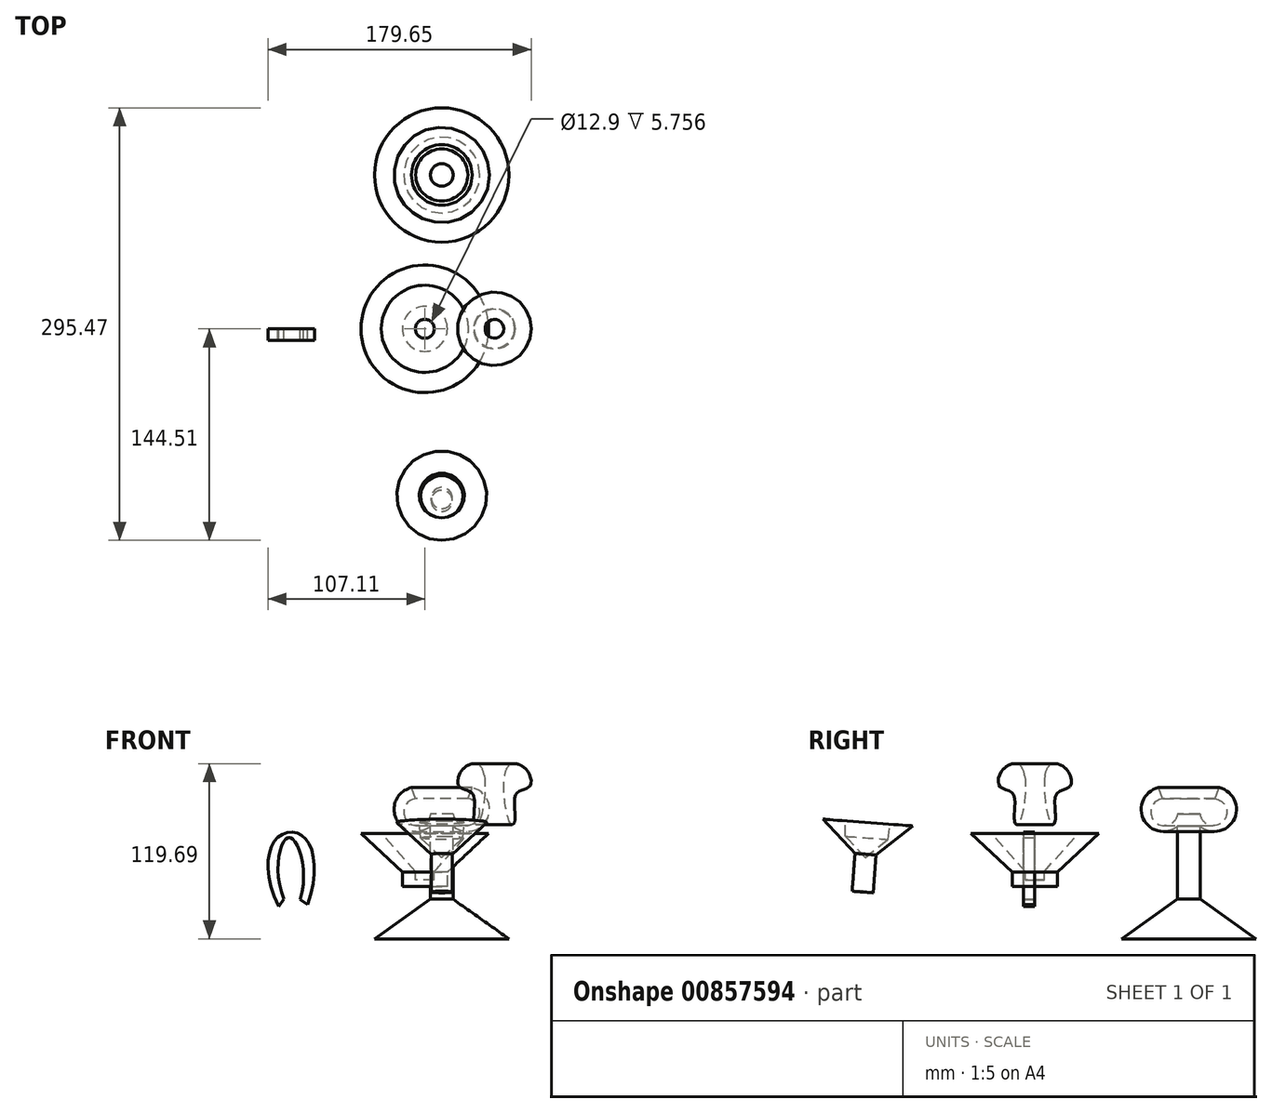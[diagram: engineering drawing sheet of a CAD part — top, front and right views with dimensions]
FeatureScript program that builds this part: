
annotation { "Feature Type Name" : "Feature", "Feature Type Description" : "" }
export const myFeature = defineFeature(function(context is Context, id is Id, definition is map)
    precondition{}
    {
        {
            var Q0;
            Q0=qCreatedBy(makeId("Front.planeOp"),FACE);
            var sketch = newSketch(context, id + "F0", { "sketchPlane" : qUnion([Q0])});
            skLineSegment(sketch, "E0", {"start": v(-55.11, 24.03) * mm, "end": v(-26.9, -2.45) * mm});
            skLineSegment(sketch, "E1", {"start": v(-26.9, -2.45) * mm, "end": v(-26.9, -12.23) * mm});
            skLineSegment(sketch, "E2", {"start": v(-26.9, -12.23) * mm, "end": v(-11.54, -12.23) * mm});
            skLineSegment(sketch, "E3", {"start": v(-11.54, 24.03) * mm, "end": v(-11.54, -12.23) * mm});
            skLineSegment(sketch, "E4", {"start": v(-55.11, 24.03) * mm, "end": v(-11.54, 24.03) * mm});
            skLineSegment(sketch, "E5", {"start": v(-41.3, 24.03) * mm, "end": v(-17.99, -2.16) * mm});
            skLineSegment(sketch, "E6", {"start": v(-17.99, -2.16) * mm, "end": v(-17.99, -7.91) * mm});
            skLineSegment(sketch, "E7", {"start": v(-17.99, -7.91) * mm, "end": v(-11.54, -7.91) * mm});
            skSolve(sketch);
        }
        {
            var Q0;
            {var subQ3=sQuery(id+"F0.wireOp",EDGE,"E0");Q0=makeQuery(id+"F0.imprint","IMPRINT",FACE,{"disambiguationData":[TD([[makeQuery(id+"F0.imprint","IMPRINT",EDGE,{"derivedFrom":subQ3}),1.0]])]});}
            var Q1;
            Q1=sQuery(id+"F0.wireOp",EDGE,"E3");
            revolve(context, id + "F1", {"surfaceOperationType" : NewSurfaceOperationType.NEW, "entities" : qUnion([Q0]), "axis" : qUnion([Q1]), "revolveType" : RevolveType.FULL});
        }
        {
            var Q0;
            Q0=qCreatedBy(makeId("Right.planeOp"),FACE);
            var sketch = newSketch(context, id + "F2", { "sketchPlane" : qUnion([Q0])});
            skLineSegment(sketch, "E8", {"start": v(-122.76, 10.3) * mm, "end": v(-124.7, -15.53) * mm});
            skLineSegment(sketch, "E9", {"start": v(-122.76, 10.3) * mm, "end": v(-144.51, 33.68) * mm});
            skLineSegment(sketch, "E10", {"start": v(-144.51, 33.68) * mm, "end": v(-113.92, 31.37) * mm});
            skLineSegment(sketch, "E11", {"start": v(-113.92, 31.37) * mm, "end": v(-117.45, -15.44) * mm});
            skLineSegment(sketch, "E12", {"start": v(-117.45, -15.44) * mm, "end": v(-124.7, -15.53) * mm});
            skLineSegment(sketch, "E13", {"start": v(-129.21, 21.99) * mm, "end": v(-126.2, 18.74) * mm});
            skPoint(sketch, "E13.startSnap0", {"position": v(-129.21, 32.52) * mm});
            skPoint(sketch, "E13.startSnap1", {"position": v(-133.64, 21.99) * mm});
            skLineSegment(sketch, "E14", {"start": v(-126.2, 18.74) * mm, "end": v(-115.72, 7.48) * mm});
            skLineSegment(sketch, "E15", {"start": v(-129.21, 21.99) * mm, "end": v(-129.21, 32.52) * mm});
            skSolve(sketch);
        }
        {
            var Q0;
            Q0=makeQuery(id+"F2.imprint","IMPRINT",FACE,{"disambiguationData":[TD([[makeQuery(id+"F2.imprint","IMPRINT",EDGE,{"derivedFrom":sQuery(id+"F2.wireOp",EDGE,"E8")}),1.0]])]});
            var Q1;
            Q1=sQuery(id+"F2.wireOp",EDGE,"E11");
            revolve(context, id + "F3", {"surfaceOperationType" : NewSurfaceOperationType.NEW, "entities" : qUnion([Q0]), "axis" : qUnion([Q1]), "revolveType" : RevolveType.FULL});
        }
        {
            var Q0;
            Q0=qCreatedBy(makeId("Front.planeOp"),FACE);
            var sketch = newSketch(context, id + "F4", { "sketchPlane" : qUnion([Q0])});
            skFitSpline(sketch, "E16", {"points": [v(57.28, 67.95) * mm, v(59.9, 56) * mm, v(50.77, 50.84) * mm, v(49.77, 32.19) * mm, v(47.37, 30.37) * mm, v(44.77, 68.93) * mm, v(57.28, 67.95) * mm]});
            skLineSegment(sketch, "E17", {"start": v(57.28, 67.95) * mm, "end": v(42.92, 63.58) * mm});
            skLineSegment(sketch, "E18", {"start": v(35.93, 70.37) * mm, "end": v(35.93, 30.65) * mm});
            skSolve(sketch);
        }
        {
            var Q0;
            Q0=makeQuery(id+"F4.imprint","IMPRINT",FACE,{"disambiguationData":[TD([[makeQuery(id+"F4.imprint","IMPRINT",EDGE,{"derivedFrom":sQuery(id+"F4.wireOp",EDGE,"E16")}),-1.0]])]});
            var Q1;
            Q1=sQuery(id+"F4.wireOp",EDGE,"E18");
            revolve(context, id + "F5", {"surfaceOperationType" : NewSurfaceOperationType.NEW, "entities" : qUnion([Q0]), "axis" : qUnion([Q1]), "revolveType" : RevolveType.FULL});
        }
        {
            var Q0;
            Q0=qCreatedBy(makeId("Right.planeOp"),FACE);
            var sketch = newSketch(context, id + "F6", { "sketchPlane" : qUnion([Q0])});
            skLineSegment(sketch, "E19", {"start": v(112.8, 28.86) * mm, "end": v(112.8, -21.04) * mm});
            skArc(sketch, "E20", {"start": v(112.8, 28.86) * mm, "mid": v(136.1, 33.73) * mm, "end": v(125.8, 55.2) * mm});
            skArc(sketch, "E21", {"start": v(112.8, 37.1) * mm, "mid": v(128.53, 32.12) * mm, "end": v(122.91, 47.63) * mm});
            skLineSegment(sketch, "E22", {"start": v(125.8, 55.2) * mm, "end": v(122.91, 47.63) * mm});
            skLineSegment(sketch, "E23", {"start": v(112.8, 37.1) * mm, "end": v(105.1, 37.1) * mm});
            skLineSegment(sketch, "E24", {"start": v(105.1, 37.1) * mm, "end": v(105.1, -48.06) * mm});
            skLineSegment(sketch, "E25", {"start": v(112.8, -21.04) * mm, "end": v(150.96, -48.06) * mm});
            skLineSegment(sketch, "E26", {"start": v(150.96, -48.06) * mm, "end": v(105.1, -48.06) * mm});
            skSolve(sketch);
        }
        {
            var Q0;
            Q0 = qSketchRegion(id + "F6", true);
            var Q1;
            Q1=sQuery(id+"F6.wireOp",EDGE,"E24");
            revolve(context, id + "F7", {"surfaceOperationType" : NewSurfaceOperationType.NEW, "entities" : qUnion([Q0]), "axis" : qUnion([Q1]), "revolveType" : RevolveType.FULL});
        }
        {
            var Q0;
            Q0=qCreatedBy(makeId("Front.planeOp"),FACE);
            var sketch = newSketch(context, id + "F8", { "sketchPlane" : qUnion([Q0])});
            skFitSpline(sketch, "E27", {"points": [v(-107.73, -21) * mm, v(-104.29, 21.14) * mm, v(-96.52, -21.28) * mm], "startDerivative": vector(-47.7, 112.83) * mm, "endDerivative": vector(-35.53, -119.47) * mm});
            skLineSegment(sketch, "E28", {"start": v(-107.73, -21) * mm, "end": v(-111.36, -25.94) * mm});
            skLineSegment(sketch, "E29", {"start": v(-96.52, -21.28) * mm, "end": v(-91.5, -24.55) * mm});
            skFitSpline(sketch, "E30", {"points": [v(-91.5, -24.55) * mm, v(-95.09, 22.27) * mm, v(-112.37, 20.7) * mm, v(-111.36, -25.94) * mm], "startDerivative": vector(60.57, 170.43) * mm, "endDerivative": vector(79.9, -161.35) * mm});
            skSolve(sketch);
        }
        {
            var Q0;
            Q0 = qSketchRegion(id + "F8", true);
            extrude(context, id + "F9", {"entities" : qUnion([Q0]), "depth" : 7.87 * mm, "offsetDistance" : 25.4 * mm});
        }
    });
